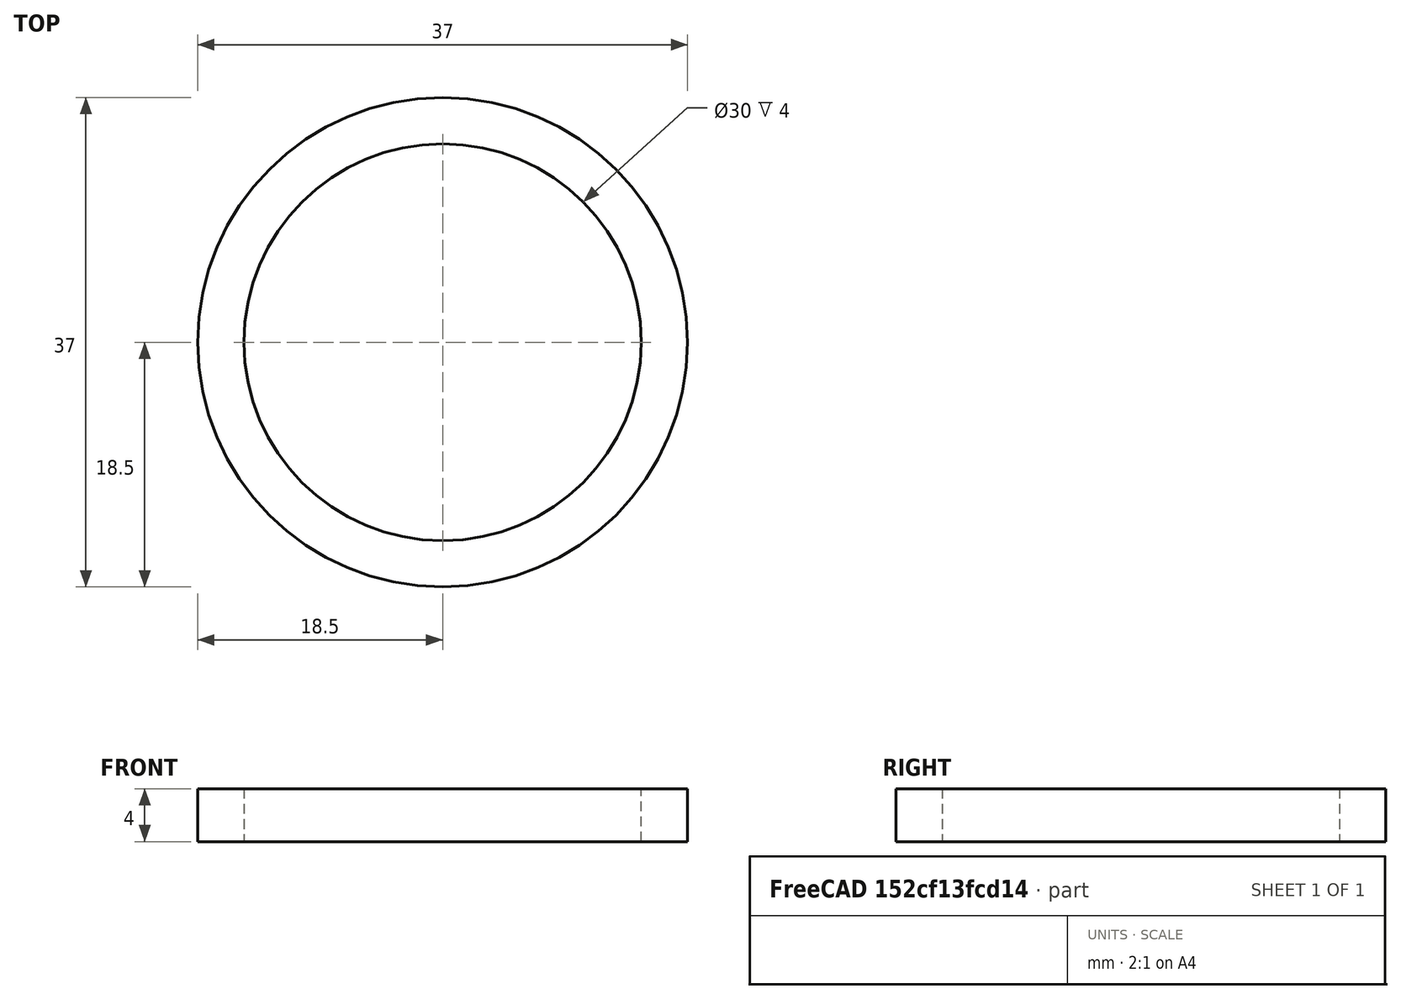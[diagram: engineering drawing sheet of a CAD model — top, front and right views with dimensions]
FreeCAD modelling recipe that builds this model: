
FCSTD DOCUMENT  (FreeCAD 0.20R29410 (Git))
Label: bearing_6706
License: All rights reserved
LicenseURL: http://en.wikipedia.org/wiki/All_rights_reserved
objects: Sketcher::SketchObject×1, PartDesign::Pad×1, PartDesign::Body×1
note: 4 computed .brp shape members not serialized (recipe doc carries the construction recipe); baked Part::Feature solids carry a one-line shape summary decoded from their .brp

FEATURE [Sketcher::SketchObject] Sketch
  FullyConstrained = true
  MapMode = 5
  Support = -> [XY_Plane]
  sketch-geometry (2):
    g0: Circle CenterX=0 CenterY=0 CenterZ=0 NormalX=0 NormalY=0 NormalZ=1 AngleXU=0 Radius=18.5
    g1: Circle CenterX=0 CenterY=0 CenterZ=0 NormalX=0 NormalY=0 NormalZ=1 AngleXU=0 Radius=15
  constraints (4):
    c: Coincident(g0,g-1)
    c: Coincident(g1,g0)
    c: Diameter(g1) = 30
    c: Diameter(g0) = 37
FEATURE [PartDesign::Pad] Pad
  Direction = (0,0,1)
  Length = 4
  Length2 = 10
  Profile = -> Sketch
  ReferenceAxis = -> Sketch [N_Axis]
  Type = 0
FEATURE [PartDesign::Body] Body
  Group = -> [Sketch,Pad]
  Origin = -> Origin
  Tip = -> Pad
